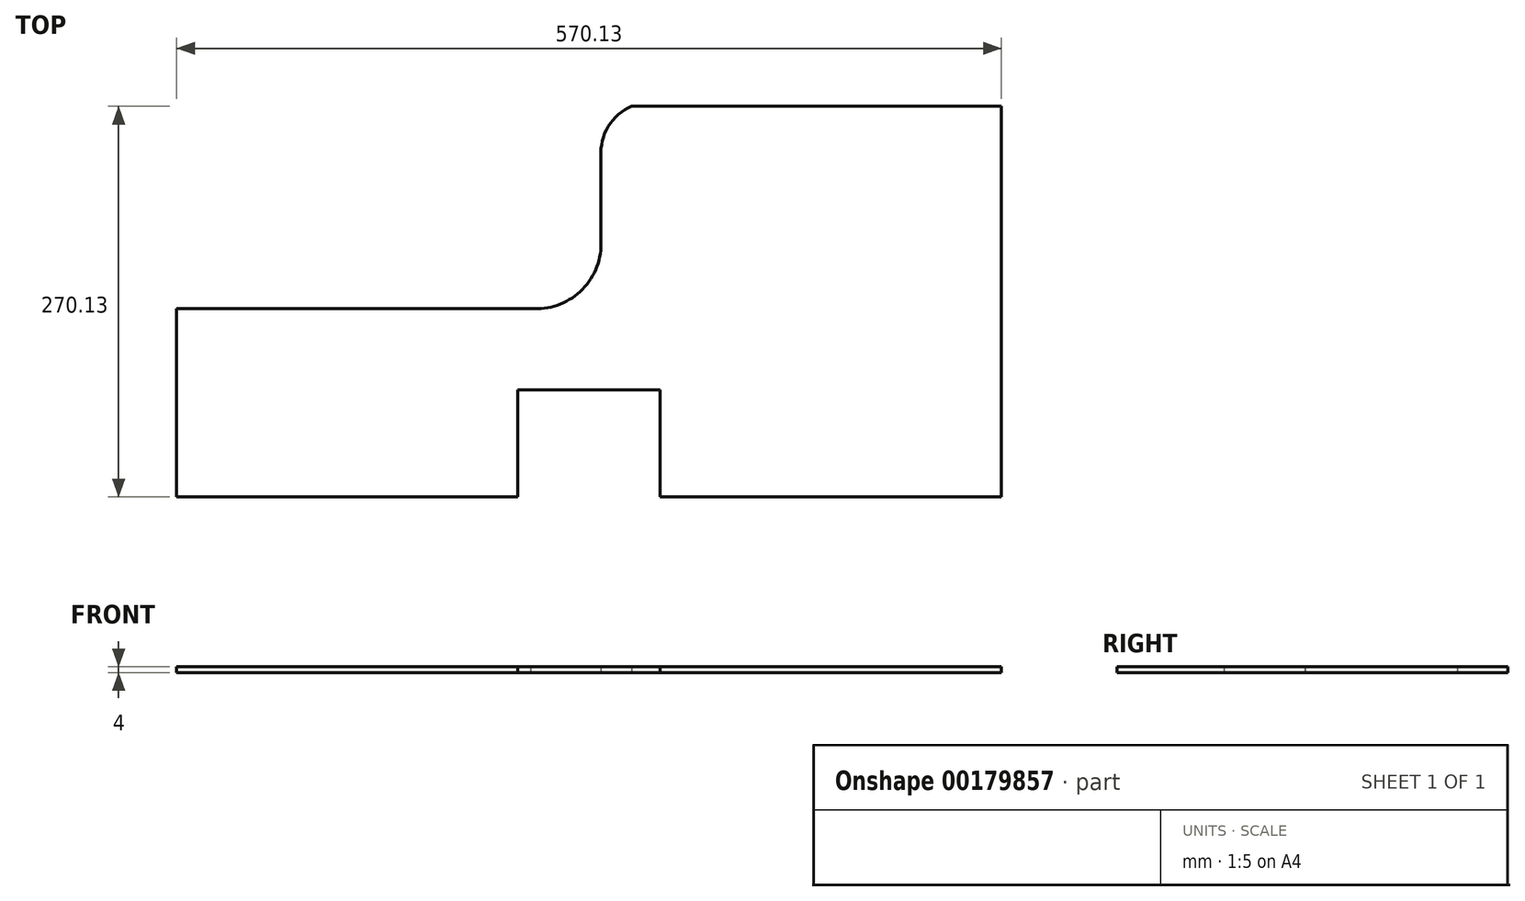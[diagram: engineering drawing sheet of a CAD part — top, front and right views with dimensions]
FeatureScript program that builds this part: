
annotation { "Feature Type Name" : "Feature", "Feature Type Description" : "" }
export const myFeature = defineFeature(function(context is Context, id is Id, definition is map)
    precondition{}
    {
        {
            var Q0;
            Q0=qCreatedBy(makeId("Top.planeOp"),FACE);
            var sketch = newSketch(context, id + "F0", { "sketchPlane" : qUnion([Q0])});
            skLineSegment(sketch, "E0", {"start": v(-296.64, -162.46) * mm, "end": v(-296.64, -22.46) * mm});
            skLineSegment(sketch, "E1", {"start": v(283.36, 117.54) * mm, "end": v(283.36, -162.46) * mm});
            skLineSegment(sketch, "E2", {"start": v(283.36, -162.46) * mm, "end": v(-296.64, -162.46) * mm});
            skLineSegment(sketch, "E3", {"start": v(-46.64, -47.62) * mm, "end": v(-46.64, 142.6) * mm, "construction": true});
            skLineSegment(sketch, "E4", {"start": v(-46.64, 17.54) * mm, "end": v(18.48, 17.54) * mm, "construction": true});
            skArc(sketch, "E5", {"start": v(-46.64, -22.46) * mm, "mid": v(-16.11, -12.03) * mm, "end": v(-3.22, 17.54) * mm});
            skLineSegment(sketch, "E6", {"start": v(-3.22, 77.54) * mm, "end": v(21.95, 77.54) * mm, "construction": true});
            skLineSegment(sketch, "E7", {"start": v(21.95, 77.54) * mm, "end": v(21.95, 117.54) * mm, "construction": true});
            skArc(sketch, "E8", {"start": v(21.95, 117.54) * mm, "mid": v(2.83, 101.65) * mm, "end": v(-3.22, 77.54) * mm});
            skLineSegment(sketch, "E9", {"start": v(-296.64, -22.46) * mm, "end": v(-46.64, -22.46) * mm});
            skLineSegment(sketch, "E10", {"start": v(-3.22, 17.54) * mm, "end": v(-3.22, 77.54) * mm});
            skLineSegment(sketch, "E11", {"start": v(21.95, 117.54) * mm, "end": v(283.36, 117.54) * mm});
            skLineSegment(sketch, "E12", {"start": v(-55.89, -162.46) * mm, "end": v(-55.89, -77.46) * mm});
            skLineSegment(sketch, "E13", {"start": v(-55.89, -77.46) * mm, "end": v(42.61, -77.46) * mm});
            skLineSegment(sketch, "E14", {"start": v(42.61, -77.46) * mm, "end": v(42.61, -162.46) * mm});
            skLineSegment(sketch, "E15", {"start": v(42.61, -162.46) * mm, "end": v(-55.89, -162.46) * mm});
            skLineSegment(sketch, "E16", {"start": v(-6.64, -77.46) * mm, "end": v(-6.64, -162.46) * mm, "construction": true});
            skLineSegment(sketch, "E17.0", {"start": v(278.43, -157.53) * mm, "end": v(-291.7, -157.53) * mm});
            skLineSegment(sketch, "E17.1", {"start": v(278.43, 112.6) * mm, "end": v(278.43, -157.53) * mm});
            skLineSegment(sketch, "E17.2", {"start": v(-291.7, -157.53) * mm, "end": v(-291.7, -27.4) * mm});
            skLineSegment(sketch, "E17.3", {"start": v(22.93, 112.6) * mm, "end": v(278.43, 112.6) * mm});
            skLineSegment(sketch, "E17.4", {"start": v(-291.7, -27.4) * mm, "end": v(-46.84, -27.4) * mm});
            skArc(sketch, "E17.5", {"start": v(-46.84, -27.4) * mm, "mid": v(-12.7, -15.59) * mm, "end": v(1.72, 17.55) * mm});
            skLineSegment(sketch, "E17.6", {"start": v(1.72, 17.55) * mm, "end": v(1.72, 77.72) * mm});
            skArc(sketch, "E17.7", {"start": v(22.93, 112.6) * mm, "mid": v(6.72, 98.57) * mm, "end": v(1.72, 77.72) * mm});
            skLineSegment(sketch, "E18.0", {"start": v(-54.89, -162.46) * mm, "end": v(-54.89, -77.46) * mm});
            skLineSegment(sketch, "E19.0", {"start": v(41.61, -77.46) * mm, "end": v(41.61, -162.46) * mm});
            skLineSegment(sketch, "E20.0", {"start": v(-55.89, -83.46) * mm, "end": v(42.61, -83.46) * mm});
            skSolve(sketch);
        }
        {
            var Q0;
            {var subQ0=sQuery(id+"F0.wireOp",EDGE,"E17.1");Q0=makeQuery(id+"F0.imprint","IMPRINT",FACE,{"disambiguationData":[TD([[makeQuery(id+"F0.imprint","IMPRINT",EDGE,{"derivedFrom":subQ0}),-1.0]])]});}
            var Q1;
            {var subQ0=sQuery(id+"F0.wireOp",EDGE,"E13");var subQ1=sQuery(id+"F0.wireOp",EDGE,"E12");var subQ2=makeQuery(id+"F0.imprint","INTERSECT",VERTEX,{"derivedFrom":[subQ1,subQ0]});Q1=makeQuery(id+"F0.imprint","IMPRINT",FACE,{"disambiguationData":[TD([[makeQuery(id+"F0.imprint","IMPRINT",EDGE,{"disambiguationData":[TD([[subQ2,1.0]])],"derivedFrom":subQ1}),-1.0]])]});}
            var Q2;
            {var subQ0=sQuery(id+"F0.wireOp",EDGE,"E14");var subQ1=sQuery(id+"F0.wireOp",EDGE,"E13");var subQ2=makeQuery(id+"F0.imprint","INTERSECT",VERTEX,{"derivedFrom":[subQ1,subQ0]});Q2=makeQuery(id+"F0.imprint","IMPRINT",FACE,{"disambiguationData":[TD([[makeQuery(id+"F0.imprint","IMPRINT",EDGE,{"disambiguationData":[TD([[subQ2,1.0]])],"derivedFrom":subQ1}),-1.0]])]});}
            var Q3;
            {var subQ0=sQuery(id+"F0.wireOp",EDGE,"E18.0");var subQ1=sQuery(id+"F0.wireOp",EDGE,"E13");var subQ2=makeQuery(id+"F0.imprint","INTERSECT",VERTEX,{"derivedFrom":[subQ1,subQ0]});Q3=makeQuery(id+"F0.imprint","IMPRINT",FACE,{"disambiguationData":[TD([[makeQuery(id+"F0.imprint","IMPRINT",EDGE,{"disambiguationData":[TD([[subQ2,-1.0]])],"derivedFrom":subQ1}),-1.0]])]});}
            extrude(context, id + "F1", {"entities" : qUnion([Q0, Q1, Q2, Q3]), "depth" : 4 * mm});
        }
    });
